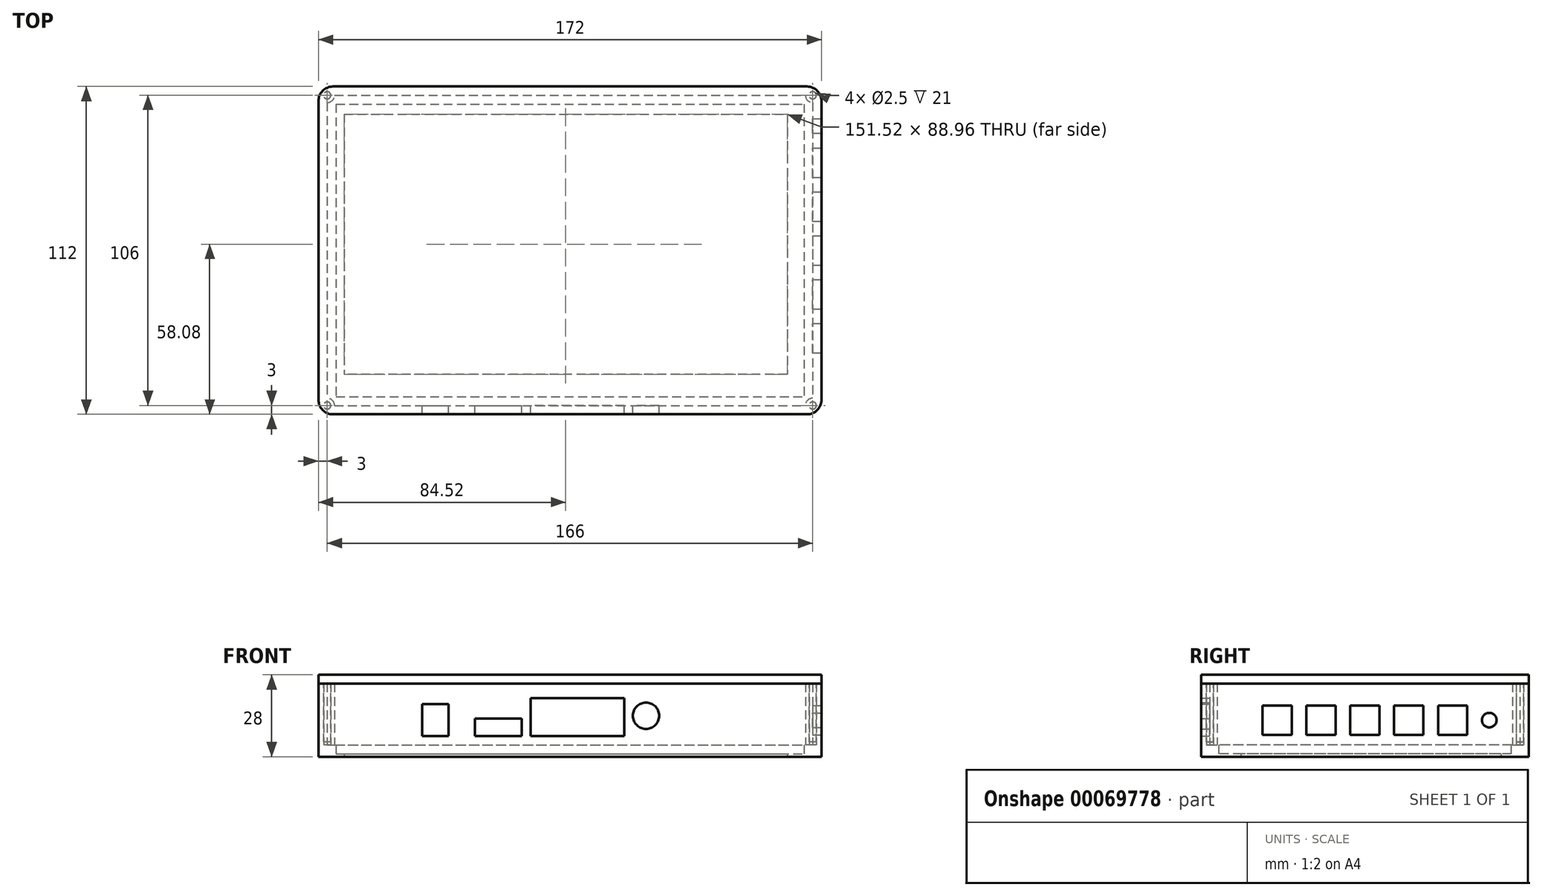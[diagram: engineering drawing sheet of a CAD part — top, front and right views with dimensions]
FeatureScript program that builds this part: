
annotation { "Feature Type Name" : "Feature", "Feature Type Description" : "" }
export const myFeature = defineFeature(function(context is Context, id is Id, definition is map)
    precondition{}
    {
        {
            var Q0;
            Q0=qCreatedBy(makeId("Top.planeOp"),FACE);
            var sketch = newSketch(context, id + "F0", { "sketchPlane" : qUnion([Q0])});
            skLineSegment(sketch, "E0.rect.bottom", {"start": v(-80, 50) * mm, "end": v(80, 50) * mm});
            skLineSegment(sketch, "E0.rect.top", {"start": v(-80, -50) * mm, "end": v(80, -50) * mm});
            skLineSegment(sketch, "E0.rect.left", {"start": v(-80, 50) * mm, "end": v(-80, -50) * mm});
            skLineSegment(sketch, "E0.rect.right", {"start": v(80, 50) * mm, "end": v(80, -50) * mm});
            skPoint(sketch, "E0.rect.middle", {"position": v(0, 0) * mm});
            skLineSegment(sketch, "E1.0", {"start": v(-81, 56) * mm, "end": v(81, 56) * mm});
            skLineSegment(sketch, "E1.1", {"start": v(-86, 51) * mm, "end": v(-86, -51) * mm});
            skLineSegment(sketch, "E1.2", {"start": v(-81, -56) * mm, "end": v(81, -56) * mm});
            skLineSegment(sketch, "E1.3", {"start": v(86, 51) * mm, "end": v(86, -51) * mm});
            skLineSegment(sketch, "E2", {"start": v(-77.24, 46.56) * mm, "end": v(74.28, 46.56) * mm});
            skLineSegment(sketch, "E3", {"start": v(74.28, 46.56) * mm, "end": v(74.28, -42.4) * mm});
            skLineSegment(sketch, "E4", {"start": v(74.28, -42.4) * mm, "end": v(-77.24, -42.4) * mm});
            skLineSegment(sketch, "E5", {"start": v(-77.24, 46.56) * mm, "end": v(-77.24, -42.4) * mm});
            skLineSegment(sketch, "E6.0", {"start": v(-80.5, 53) * mm, "end": v(80.5, 53) * mm});
            skLineSegment(sketch, "E6.1", {"start": v(-83, 50.5) * mm, "end": v(-83, -50.5) * mm});
            skLineSegment(sketch, "E6.2", {"start": v(-80.5, -53) * mm, "end": v(80.5, -53) * mm});
            skLineSegment(sketch, "E6.3", {"start": v(83, 50.5) * mm, "end": v(83, -50.5) * mm});
            skPoint(sketch, "E7.visualSharp", {"position": v(-86, 56) * mm});
            skArc(sketch, "E7.filletArc", {"start": v(-81, 56) * mm, "mid": v(-84.54, 54.54) * mm, "end": v(-86, 51) * mm});
            skPoint(sketch, "E8.visualSharp", {"position": v(86, 56) * mm});
            skArc(sketch, "E8.filletArc", {"start": v(86, 51) * mm, "mid": v(84.54, 54.54) * mm, "end": v(81, 56) * mm});
            skPoint(sketch, "E9.visualSharp", {"position": v(86, -56) * mm});
            skArc(sketch, "E9.filletArc", {"start": v(81, -56) * mm, "mid": v(84.54, -54.54) * mm, "end": v(86, -51) * mm});
            skPoint(sketch, "E10.visualSharp", {"position": v(-86, -56) * mm});
            skArc(sketch, "E10.filletArc", {"start": v(-86, -51) * mm, "mid": v(-84.54, -54.54) * mm, "end": v(-81, -56) * mm});
            skPoint(sketch, "E11.visualSharp", {"position": v(-83, 53) * mm});
            skPoint(sketch, "E12.visualSharp", {"position": v(83, 53) * mm});
            skPoint(sketch, "E13.visualSharp", {"position": v(83, -53) * mm});
            skPoint(sketch, "E14.visualSharp", {"position": v(-83, -53) * mm});
            skLineSegment(sketch, "E15", {"start": v(-86, -50) * mm, "end": v(-80, -50) * mm, "construction": true});
            skLineSegment(sketch, "E16", {"start": v(-80, -50) * mm, "end": v(-80, -56) * mm, "construction": true});
            skLineSegment(sketch, "E17", {"start": v(-80, -53) * mm, "end": v(-83, -53) * mm, "construction": true});
            skPoint(sketch, "E17.endSnap0", {"position": v(-83, -50) * mm});
            skLineSegment(sketch, "E18", {"start": v(-83, -53) * mm, "end": v(-83, -50) * mm, "construction": true});
            skArc(sketch, "E19", {"start": v(-80.5, -53) * mm, "mid": v(-81.23, -51.23) * mm, "end": v(-83, -50.5) * mm});
            skCircle(sketch, "E20.0", {"center": v(-83, -53) * mm, "radius": 1.25 * mm});
            skLineSegment(sketch, "E21", {"start": v(-80, 50) * mm, "end": v(-80, 56) * mm, "construction": true});
            skLineSegment(sketch, "E22", {"start": v(-80, 50) * mm, "end": v(-86, 50) * mm, "construction": true});
            skLineSegment(sketch, "E23", {"start": v(-83, 50) * mm, "end": v(-83, 53) * mm, "construction": true});
            skPoint(sketch, "E23.endSnap0", {"position": v(-80, 53) * mm});
            skArc(sketch, "E24", {"start": v(-83, 50.5) * mm, "mid": v(-81.23, 51.23) * mm, "end": v(-80.5, 53) * mm});
            skCircle(sketch, "E25.0", {"center": v(-83, 53) * mm, "radius": 1.25 * mm});
            skLineSegment(sketch, "E26", {"start": v(80, 50) * mm, "end": v(80, 56) * mm, "construction": true});
            skLineSegment(sketch, "E27", {"start": v(80, 50) * mm, "end": v(86, 50) * mm, "construction": true});
            skLineSegment(sketch, "E28", {"start": v(83, 50) * mm, "end": v(83, 53) * mm, "construction": true});
            skPoint(sketch, "E28.endSnap0", {"position": v(80, 53) * mm});
            skLineSegment(sketch, "E29", {"start": v(80, -50) * mm, "end": v(80, -56) * mm, "construction": true});
            skLineSegment(sketch, "E30", {"start": v(80, -50) * mm, "end": v(86, -50) * mm, "construction": true});
            skLineSegment(sketch, "E31", {"start": v(83, -50) * mm, "end": v(83, -53) * mm, "construction": true});
            skPoint(sketch, "E31.endSnap0", {"position": v(80, -53) * mm});
            skArc(sketch, "E32", {"start": v(80.5, 53) * mm, "mid": v(81.23, 51.23) * mm, "end": v(83, 50.5) * mm});
            skArc(sketch, "E33", {"start": v(83, -50.5) * mm, "mid": v(81.23, -51.23) * mm, "end": v(80.5, -53) * mm});
            skCircle(sketch, "E34.0", {"center": v(83, 53) * mm, "radius": 1.25 * mm});
            skCircle(sketch, "E35.0", {"center": v(83, -53) * mm, "radius": 1.25 * mm});
            skLineSegment(sketch, "E36", {"start": v(-80.5, -53) * mm, "end": v(-80.5, -53) * mm});
            skLineSegment(sketch, "E37", {"start": v(-83, -50.5) * mm, "end": v(-83, -50.5) * mm});
            skLineSegment(sketch, "E38", {"start": v(-83, 50.5) * mm, "end": v(-83, 50.5) * mm});
            skLineSegment(sketch, "E39", {"start": v(-83, 53) * mm, "end": v(-80, 53) * mm, "construction": true});
            skLineSegment(sketch, "E40", {"start": v(-80.5, 53) * mm, "end": v(-80.5, 53) * mm});
            skLineSegment(sketch, "E41", {"start": v(83, -53) * mm, "end": v(80, -53) * mm, "construction": true});
            skLineSegment(sketch, "E42", {"start": v(83, -50.5) * mm, "end": v(83, -50.5) * mm});
            skLineSegment(sketch, "E43", {"start": v(80.5, -53) * mm, "end": v(80.5, -53) * mm});
            skLineSegment(sketch, "E44", {"start": v(80, 53) * mm, "end": v(83, 53) * mm, "construction": true});
            skLineSegment(sketch, "E45", {"start": v(83, 50.5) * mm, "end": v(83, 50.5) * mm});
            skLineSegment(sketch, "E46", {"start": v(80.5, 53) * mm, "end": v(80.5, 53) * mm});
            skSolve(sketch);
        }
        {
            var Q0;
            Q0=makeQuery(id+"F0.imprint","IMPRINT",FACE,{"disambiguationData":[TD([[makeQuery(id+"F0.imprint","IMPRINT",EDGE,{"derivedFrom":sQuery(id+"F0.wireOp",EDGE,"E0.rect.bottom")}),-1.0]])]});
            extrude(context, id + "F1", {"entities" : qUnion([Q0]), "depth" : 1 * mm});
        }
        {
            var Q0;
            Q0=makeQuery(id+"F0.imprint","IMPRINT",FACE,{"disambiguationData":[TD([[makeQuery(id+"F0.imprint","IMPRINT",EDGE,{"derivedFrom":sQuery(id+"F0.wireOp",EDGE,"E0.rect.bottom")}),1.0]])]});
            extrude(context, id + "F2", {"entities" : qUnion([Q0]), "operationType" : NewBodyOperationType.ADD, "depth" : 4 * mm});
        }
        {
            var Q0;
            Q0=makeQuery(id+"F0.imprint","IMPRINT",FACE,{"disambiguationData":[TD([[makeQuery(id+"F0.imprint","IMPRINT",EDGE,{"derivedFrom":sQuery(id+"F0.wireOp",EDGE,"E1.0")}),-1.0]])]});
            extrude(context, id + "F3", {"entities" : qUnion([Q0]), "operationType" : NewBodyOperationType.ADD, "depth" : 25 * mm});
        }
        {
            var Q0;
            Q0=makeQuery(id+"F0.imprint","IMPRINT",FACE,{"disambiguationData":[TD([[makeQuery(id+"F0.imprint","IMPRINT",EDGE,{"derivedFrom":sQuery(id+"F0.wireOp",EDGE,"E25.0")}),1.0]])]});
            extrude(context, id + "F4", {"entities" : qUnion([Q0]), "operationType" : NewBodyOperationType.ADD, "depth" : 4 * mm});
        }
        {
            var Q0;
            Q0=makeQuery(id+"F0.imprint","IMPRINT",FACE,{"disambiguationData":[TD([[makeQuery(id+"F0.imprint","IMPRINT",EDGE,{"derivedFrom":sQuery(id+"F0.wireOp",EDGE,"E20.0")}),1.0]])]});
            extrude(context, id + "F5", {"entities" : qUnion([Q0]), "operationType" : NewBodyOperationType.ADD, "depth" : 4 * mm});
        }
        {
            var Q0;
            Q0=makeQuery(id+"F0.imprint","IMPRINT",FACE,{"disambiguationData":[TD([[makeQuery(id+"F0.imprint","IMPRINT",EDGE,{"derivedFrom":sQuery(id+"F0.wireOp",EDGE,"E35.0")}),1.0]])]});
            extrude(context, id + "F6", {"entities" : qUnion([Q0]), "operationType" : NewBodyOperationType.ADD, "depth" : 4 * mm});
        }
        {
            var Q0;
            Q0=makeQuery(id+"F0.imprint","IMPRINT",FACE,{"disambiguationData":[TD([[makeQuery(id+"F0.imprint","IMPRINT",EDGE,{"derivedFrom":sQuery(id+"F0.wireOp",EDGE,"E34.0")}),1.0]])]});
            extrude(context, id + "F7", {"entities" : qUnion([Q0]), "operationType" : NewBodyOperationType.ADD, "depth" : 4 * mm});
        }
        {
            var Q0;
            Q0=makeQuery(id+"F3.opExtrude","SWEPT_FACE",FACE,{"disambiguationData":[OSD([sQuery(id+"F0.wireOp",EDGE,"E6.2")])]});
            var sketch = newSketch(context, id + "F8", { "sketchPlane" : qUnion([Q0])});
            skLineSegment(sketch, "E47.0.0", {"start": v(-80.5, 4) * mm, "end": v(80.5, 4) * mm});
            skLineSegment(sketch, "E47.0.1", {"start": v(80.5, 4) * mm, "end": v(80.5, 25) * mm});
            skLineSegment(sketch, "E47.0.2", {"start": v(80.5, 25) * mm, "end": v(-80.5, 25) * mm});
            skLineSegment(sketch, "E47.0.3", {"start": v(-80.5, 25) * mm, "end": v(-80.5, 4) * mm});
            skLineSegment(sketch, "E48", {"start": v(80.5, 4) * mm, "end": v(80.5, 7) * mm, "construction": true});
            skLineSegment(sketch, "E49", {"start": v(80.5, 7) * mm, "end": v(-80.5, 7) * mm, "construction": true});
            skLineSegment(sketch, "E50", {"start": v(50.5, 7) * mm, "end": v(50.5, 4) * mm, "construction": true});
            skLineSegment(sketch, "E51", {"start": v(50.5, 7) * mm, "end": v(41.5, 7) * mm});
            skLineSegment(sketch, "E52", {"start": v(50.5, 7) * mm, "end": v(50.5, 18) * mm});
            skLineSegment(sketch, "E53", {"start": v(50.5, 18) * mm, "end": v(41.5, 18) * mm});
            skLineSegment(sketch, "E54", {"start": v(41.5, 18) * mm, "end": v(41.5, 7) * mm});
            skLineSegment(sketch, "E55", {"start": v(41.5, 7) * mm, "end": v(32.5, 7) * mm, "construction": true});
            skLineSegment(sketch, "E56", {"start": v(32.5, 7) * mm, "end": v(16.5, 7) * mm});
            skLineSegment(sketch, "E57", {"start": v(32.5, 7) * mm, "end": v(32.5, 13) * mm});
            skLineSegment(sketch, "E58", {"start": v(32.5, 13) * mm, "end": v(16.5, 13) * mm});
            skLineSegment(sketch, "E59", {"start": v(16.5, 13) * mm, "end": v(16.5, 7) * mm});
            skLineSegment(sketch, "E60", {"start": v(13.5, 7) * mm, "end": v(13.5, 20) * mm});
            skLineSegment(sketch, "E61", {"start": v(13.5, 20) * mm, "end": v(-18.5, 20) * mm});
            skLineSegment(sketch, "E62", {"start": v(-18.5, 20) * mm, "end": v(-18.5, 7) * mm});
            skLineSegment(sketch, "E63", {"start": v(-18.5, 7) * mm, "end": v(13.5, 7) * mm});
            skLineSegment(sketch, "E64", {"start": v(-26, 7) * mm, "end": v(-26, 14) * mm, "construction": true});
            skCircle(sketch, "E65", {"center": v(-26, 14) * mm, "radius": 4.5 * mm});
            skSolve(sketch);
        }
        {
            var Q0;
            Q0=makeQuery(id+"F8.imprint","IMPRINT",FACE,{"disambiguationData":[TD([[makeQuery(id+"F8.imprint","IMPRINT",EDGE,{"derivedFrom":sQuery(id+"F8.wireOp",EDGE,"E51")}),-1.0]])]});
            var Q1;
            Q1=makeQuery(id+"F8.imprint","IMPRINT",FACE,{"disambiguationData":[TD([[makeQuery(id+"F8.imprint","IMPRINT",EDGE,{"derivedFrom":sQuery(id+"F8.wireOp",EDGE,"E56")}),-1.0]])]});
            var Q2;
            Q2=makeQuery(id+"F8.imprint","IMPRINT",FACE,{"disambiguationData":[TD([[makeQuery(id+"F8.imprint","IMPRINT",EDGE,{"derivedFrom":sQuery(id+"F8.wireOp",EDGE,"E60")}),1.0]])]});
            var Q3;
            Q3=makeQuery(id+"F8.imprint","IMPRINT",FACE,{"disambiguationData":[TD([[makeQuery(id+"F8.imprint","IMPRINT",EDGE,{"derivedFrom":sQuery(id+"F8.wireOp",EDGE,"E65")}),1.0]])]});
            extrude(context, id + "F9", {"entities" : qUnion([Q0, Q1, Q2, Q3]), "operationType" : NewBodyOperationType.REMOVE, "oppositeDirection" : true, "depth" : 25 * mm});
        }
        {
            var Q0;
            Q0=makeQuery(id+"F3.opExtrude","CAP_FACE",FACE,{"disambiguationData":[OSD([sQuery(id+"F0.wireOp",EDGE,"E1.0"),sQuery(id+"F0.wireOp",EDGE,"E1.1"),sQuery(id+"F0.wireOp",EDGE,"E1.2"),sQuery(id+"F0.wireOp",EDGE,"E1.3"),sQuery(id+"F0.wireOp",EDGE,"E6.0"),sQuery(id+"F0.wireOp",EDGE,"E6.1"),sQuery(id+"F0.wireOp",EDGE,"E6.2"),sQuery(id+"F0.wireOp",EDGE,"E6.3"),sQuery(id+"F0.wireOp",EDGE,"E7.filletArc"),sQuery(id+"F0.wireOp",EDGE,"E8.filletArc"),sQuery(id+"F0.wireOp",EDGE,"E9.filletArc"),sQuery(id+"F0.wireOp",EDGE,"E10.filletArc"),sQuery(id+"F0.wireOp",EDGE,"E19"),sQuery(id+"F0.wireOp",EDGE,"E20.0"),sQuery(id+"F0.wireOp",EDGE,"E24"),sQuery(id+"F0.wireOp",EDGE,"E25.0"),sQuery(id+"F0.wireOp",EDGE,"E32"),sQuery(id+"F0.wireOp",EDGE,"E33"),sQuery(id+"F0.wireOp",EDGE,"E34.0"),sQuery(id+"F0.wireOp",EDGE,"E35.0")])],"isStart":false});
            cPlane(context, id + "F10", {"entities" : qUnion([Q0]), "cplaneType" : CPlaneType.OFFSET, "offset" : 0 * mm, "width" : 150 * mm, "height" : 150 * mm});
        }
        {
            var Q0;
            Q0=qCreatedBy(id+"F10.planeOp",FACE);
            var sketch = newSketch(context, id + "F11", { "sketchPlane" : qUnion([Q0])});
            skLineSegment(sketch, "E66.rect.bottom", {"start": v(81, 56) * mm, "end": v(-81, 56) * mm});
            skLineSegment(sketch, "E66.rect.top", {"start": v(81, -56) * mm, "end": v(-81, -56) * mm});
            skLineSegment(sketch, "E66.rect.left", {"start": v(86, 51) * mm, "end": v(86, -51) * mm});
            skLineSegment(sketch, "E66.rect.right", {"start": v(-86, 51) * mm, "end": v(-86, -51) * mm});
            skPoint(sketch, "E66.rect.middle", {"position": v(0, 0) * mm});
            skPoint(sketch, "E67.visualSharp", {"position": v(86, -56) * mm});
            skArc(sketch, "E67.filletArc", {"start": v(81, -56) * mm, "mid": v(84.54, -54.54) * mm, "end": v(86, -51) * mm});
            skPoint(sketch, "E68.visualSharp", {"position": v(86, 56) * mm});
            skArc(sketch, "E68.filletArc", {"start": v(86, 51) * mm, "mid": v(84.54, 54.54) * mm, "end": v(81, 56) * mm});
            skPoint(sketch, "E69.visualSharp", {"position": v(-86, -56) * mm});
            skArc(sketch, "E69.filletArc", {"start": v(-86, -51) * mm, "mid": v(-84.54, -54.54) * mm, "end": v(-81, -56) * mm});
            skPoint(sketch, "E70.visualSharp", {"position": v(-86, 56) * mm});
            skArc(sketch, "E70.filletArc", {"start": v(-81, 56) * mm, "mid": v(-84.54, 54.54) * mm, "end": v(-86, 51) * mm});
            skLineSegment(sketch, "E71", {"start": v(-81, -56) * mm, "end": v(-81, -51) * mm, "construction": true});
            skLineSegment(sketch, "E72", {"start": v(-86, -51) * mm, "end": v(-81, -51) * mm, "construction": true});
            skLineSegment(sketch, "E73", {"start": v(-83, -51) * mm, "end": v(-83, -53) * mm, "construction": true});
            skLineSegment(sketch, "E74", {"start": v(-83, -53) * mm, "end": v(-81, -53) * mm, "construction": true});
            skCircle(sketch, "E75", {"center": v(-83, -53) * mm, "radius": 1.2 * mm});
            skLineSegment(sketch, "E76", {"start": v(-81, 51) * mm, "end": v(-83, 51) * mm, "construction": true});
            skLineSegment(sketch, "E77", {"start": v(-83, 51) * mm, "end": v(-83, 53) * mm, "construction": true});
            skLineSegment(sketch, "E78", {"start": v(-83, 53) * mm, "end": v(-81, 53) * mm, "construction": true});
            skLineSegment(sketch, "E79", {"start": v(-81, 53) * mm, "end": v(-81, 51) * mm, "construction": true});
            skCircle(sketch, "E80", {"center": v(-83, 53) * mm, "radius": 1.2 * mm});
            skLineSegment(sketch, "E81", {"start": v(81, 51) * mm, "end": v(81, 53) * mm, "construction": true});
            skLineSegment(sketch, "E82", {"start": v(81, 53) * mm, "end": v(83, 53) * mm, "construction": true});
            skLineSegment(sketch, "E83", {"start": v(83, 53) * mm, "end": v(83, 51) * mm, "construction": true});
            skLineSegment(sketch, "E84", {"start": v(83, 51) * mm, "end": v(81, 51) * mm, "construction": true});
            skCircle(sketch, "E85", {"center": v(83, 53) * mm, "radius": 1.2 * mm});
            skLineSegment(sketch, "E86", {"start": v(81, -51) * mm, "end": v(83, -51) * mm, "construction": true});
            skLineSegment(sketch, "E87", {"start": v(83, -51) * mm, "end": v(83, -53) * mm, "construction": true});
            skLineSegment(sketch, "E88", {"start": v(83, -53) * mm, "end": v(81, -53) * mm, "construction": true});
            skLineSegment(sketch, "E89", {"start": v(81, -53) * mm, "end": v(81, -51) * mm, "construction": true});
            skCircle(sketch, "E90", {"center": v(83, -53) * mm, "radius": 1.2 * mm});
            skSolve(sketch);
        }
        {
            var Q0;
            Q0=makeQuery(id+"F11.imprint","IMPRINT",FACE,{"disambiguationData":[TD([[makeQuery(id+"F11.imprint","IMPRINT",EDGE,{"derivedFrom":sQuery(id+"F11.wireOp",EDGE,"E66.rect.bottom")}),1.0]])]});
            var Q1;
            Q1=makeQuery(id+"F11.imprint","IMPRINT",FACE,{"disambiguationData":[TD([[makeQuery(id+"F11.imprint","IMPRINT",EDGE,{"derivedFrom":sQuery(id+"F11.wireOp",EDGE,"E75")}),1.0]])]});
            var Q2;
            Q2=makeQuery(id+"F11.imprint","IMPRINT",FACE,{"disambiguationData":[TD([[makeQuery(id+"F11.imprint","IMPRINT",EDGE,{"derivedFrom":sQuery(id+"F11.wireOp",EDGE,"E90")}),1.0]])]});
            var Q3;
            Q3=makeQuery(id+"F11.imprint","IMPRINT",FACE,{"disambiguationData":[TD([[makeQuery(id+"F11.imprint","IMPRINT",EDGE,{"derivedFrom":sQuery(id+"F11.wireOp",EDGE,"E85")}),1.0]])]});
            var Q4;
            Q4=makeQuery(id+"F11.imprint","IMPRINT",FACE,{"disambiguationData":[TD([[makeQuery(id+"F11.imprint","IMPRINT",EDGE,{"derivedFrom":sQuery(id+"F11.wireOp",EDGE,"E80")}),1.0]])]});
            extrude(context, id + "F12", {"entities" : qUnion([Q0, Q1, Q2, Q3, Q4]), "depth" : 3 * mm});
        }
        {
            var Q0;
            Q0=makeQuery(id+"F11.imprint","IMPRINT",FACE,{"disambiguationData":[TD([[makeQuery(id+"F11.imprint","IMPRINT",EDGE,{"derivedFrom":sQuery(id+"F11.wireOp",EDGE,"E80")}),1.0]])]});
            var Q1;
            Q1=makeQuery(id+"F11.imprint","IMPRINT",FACE,{"disambiguationData":[TD([[makeQuery(id+"F11.imprint","IMPRINT",EDGE,{"derivedFrom":sQuery(id+"F11.wireOp",EDGE,"E85")}),1.0]])]});
            var Q2;
            Q2=makeQuery(id+"F11.imprint","IMPRINT",FACE,{"disambiguationData":[TD([[makeQuery(id+"F11.imprint","IMPRINT",EDGE,{"derivedFrom":sQuery(id+"F11.wireOp",EDGE,"E90")}),1.0]])]});
            var Q3;
            Q3=makeQuery(id+"F11.imprint","IMPRINT",FACE,{"disambiguationData":[TD([[makeQuery(id+"F11.imprint","IMPRINT",EDGE,{"derivedFrom":sQuery(id+"F11.wireOp",EDGE,"E75")}),1.0]])]});
            extrude(context, id + "F13", {"entities" : qUnion([Q0, Q1, Q2, Q3]), "operationType" : NewBodyOperationType.ADD, "oppositeDirection" : true, "depth" : 20 * mm});
        }
        {
            var Q0;
            Q0=makeQuery(id+"F3.opExtrude","SWEPT_FACE",FACE,{"disambiguationData":[OSD([sQuery(id+"F0.wireOp",EDGE,"E1.3")])]});
            var sketch = newSketch(context, id + "F14", { "sketchPlane" : qUnion([Q0])});
            skLineSegment(sketch, "E91.rect.bottom", {"start": v(5, 17.5) * mm, "end": v(-5, 17.5) * mm});
            skLineSegment(sketch, "E91.rect.top", {"start": v(5, 7.5) * mm, "end": v(-5, 7.5) * mm});
            skLineSegment(sketch, "E91.rect.left", {"start": v(5, 17.5) * mm, "end": v(5, 7.5) * mm});
            skLineSegment(sketch, "E91.rect.right", {"start": v(-5, 17.5) * mm, "end": v(-5, 7.5) * mm});
            skPoint(sketch, "E91.rect.middle", {"position": v(0, 12.5) * mm});
            skPoint(sketch, "E91.rect.middle.positionSnap0", {"position": v(-51, 12.5) * mm});
            skPoint(sketch, "E91.rect.centerSnap0", {"position": v(-51, 12.5) * mm});
            skLineSegment(sketch, "E92.rect.bottom", {"start": v(10, 17.5) * mm, "end": v(20, 17.5) * mm});
            skLineSegment(sketch, "E92.rect.top", {"start": v(10, 7.5) * mm, "end": v(20, 7.5) * mm});
            skLineSegment(sketch, "E92.rect.left", {"start": v(10, 17.5) * mm, "end": v(10, 7.5) * mm});
            skLineSegment(sketch, "E92.rect.right", {"start": v(20, 17.5) * mm, "end": v(20, 7.5) * mm});
            skPoint(sketch, "E92.rect.middle", {"position": v(15, 12.5) * mm});
            skLineSegment(sketch, "E93.rect.bottom", {"start": v(25, 17.5) * mm, "end": v(35, 17.5) * mm});
            skLineSegment(sketch, "E93.rect.top", {"start": v(25, 7.5) * mm, "end": v(35, 7.5) * mm});
            skLineSegment(sketch, "E93.rect.left", {"start": v(25, 17.5) * mm, "end": v(25, 7.5) * mm});
            skLineSegment(sketch, "E93.rect.right", {"start": v(35, 17.5) * mm, "end": v(35, 7.5) * mm});
            skPoint(sketch, "E93.rect.middle", {"position": v(30, 12.5) * mm});
            skLineSegment(sketch, "E94.rect.bottom", {"start": v(-20, 17.5) * mm, "end": v(-10, 17.5) * mm});
            skLineSegment(sketch, "E94.rect.top", {"start": v(-20, 7.5) * mm, "end": v(-10, 7.5) * mm});
            skLineSegment(sketch, "E94.rect.left", {"start": v(-20, 17.5) * mm, "end": v(-20, 7.5) * mm});
            skLineSegment(sketch, "E94.rect.right", {"start": v(-10, 17.5) * mm, "end": v(-10, 7.5) * mm});
            skPoint(sketch, "E94.rect.middle", {"position": v(-15, 12.5) * mm});
            skPoint(sketch, "E94.rect.middle.positionSnap0", {"position": v(-5, 12.5) * mm});
            skPoint(sketch, "E94.rect.centerSnap0", {"position": v(-5, 12.5) * mm});
            skLineSegment(sketch, "E95.rect.bottom", {"start": v(-35, 17.5) * mm, "end": v(-25, 17.5) * mm});
            skLineSegment(sketch, "E95.rect.top", {"start": v(-35, 7.5) * mm, "end": v(-25, 7.5) * mm});
            skLineSegment(sketch, "E95.rect.left", {"start": v(-35, 17.5) * mm, "end": v(-35, 7.5) * mm});
            skLineSegment(sketch, "E95.rect.right", {"start": v(-25, 17.5) * mm, "end": v(-25, 7.5) * mm});
            skPoint(sketch, "E95.rect.middle", {"position": v(-30, 12.5) * mm});
            skPoint(sketch, "E95.rect.middle.positionSnap0", {"position": v(-20, 12.5) * mm});
            skPoint(sketch, "E95.rect.centerSnap0", {"position": v(-20, 12.5) * mm});
            skCircle(sketch, "E96", {"center": v(42.5, 12.5) * mm, "radius": 2.5 * mm});
            skPoint(sketch, "E96.centerSnap0", {"position": v(35, 12.5) * mm});
            skSolve(sketch);
        }
        {
            var Q0;
            Q0=makeQuery(id+"F14.imprint","IMPRINT",FACE,{"disambiguationData":[TD([[makeQuery(id+"F14.imprint","IMPRINT",EDGE,{"derivedFrom":sQuery(id+"F14.wireOp",EDGE,"E95.rect.bottom")}),-1.0]])]});
            var Q1;
            Q1=makeQuery(id+"F14.imprint","IMPRINT",FACE,{"disambiguationData":[TD([[makeQuery(id+"F14.imprint","IMPRINT",EDGE,{"derivedFrom":sQuery(id+"F14.wireOp",EDGE,"E94.rect.bottom")}),-1.0]])]});
            var Q2;
            Q2=makeQuery(id+"F14.imprint","IMPRINT",FACE,{"disambiguationData":[TD([[makeQuery(id+"F14.imprint","IMPRINT",EDGE,{"derivedFrom":sQuery(id+"F14.wireOp",EDGE,"E91.rect.bottom")}),1.0]])]});
            var Q3;
            Q3=makeQuery(id+"F14.imprint","IMPRINT",FACE,{"disambiguationData":[TD([[makeQuery(id+"F14.imprint","IMPRINT",EDGE,{"derivedFrom":sQuery(id+"F14.wireOp",EDGE,"E92.rect.bottom")}),-1.0]])]});
            var Q4;
            Q4=makeQuery(id+"F14.imprint","IMPRINT",FACE,{"disambiguationData":[TD([[makeQuery(id+"F14.imprint","IMPRINT",EDGE,{"derivedFrom":sQuery(id+"F14.wireOp",EDGE,"E93.rect.bottom")}),-1.0]])]});
            var Q5;
            Q5=makeQuery(id+"F14.imprint","IMPRINT",FACE,{"disambiguationData":[TD([[makeQuery(id+"F14.imprint","IMPRINT",EDGE,{"derivedFrom":sQuery(id+"F14.wireOp",EDGE,"E96")}),1.0]])]});
            extrude(context, id + "F15", {"entities" : qUnion([Q0, Q1, Q2, Q3, Q4, Q5]), "operationType" : NewBodyOperationType.REMOVE, "oppositeDirection" : true, "depth" : 25 * mm});
        }
    });
